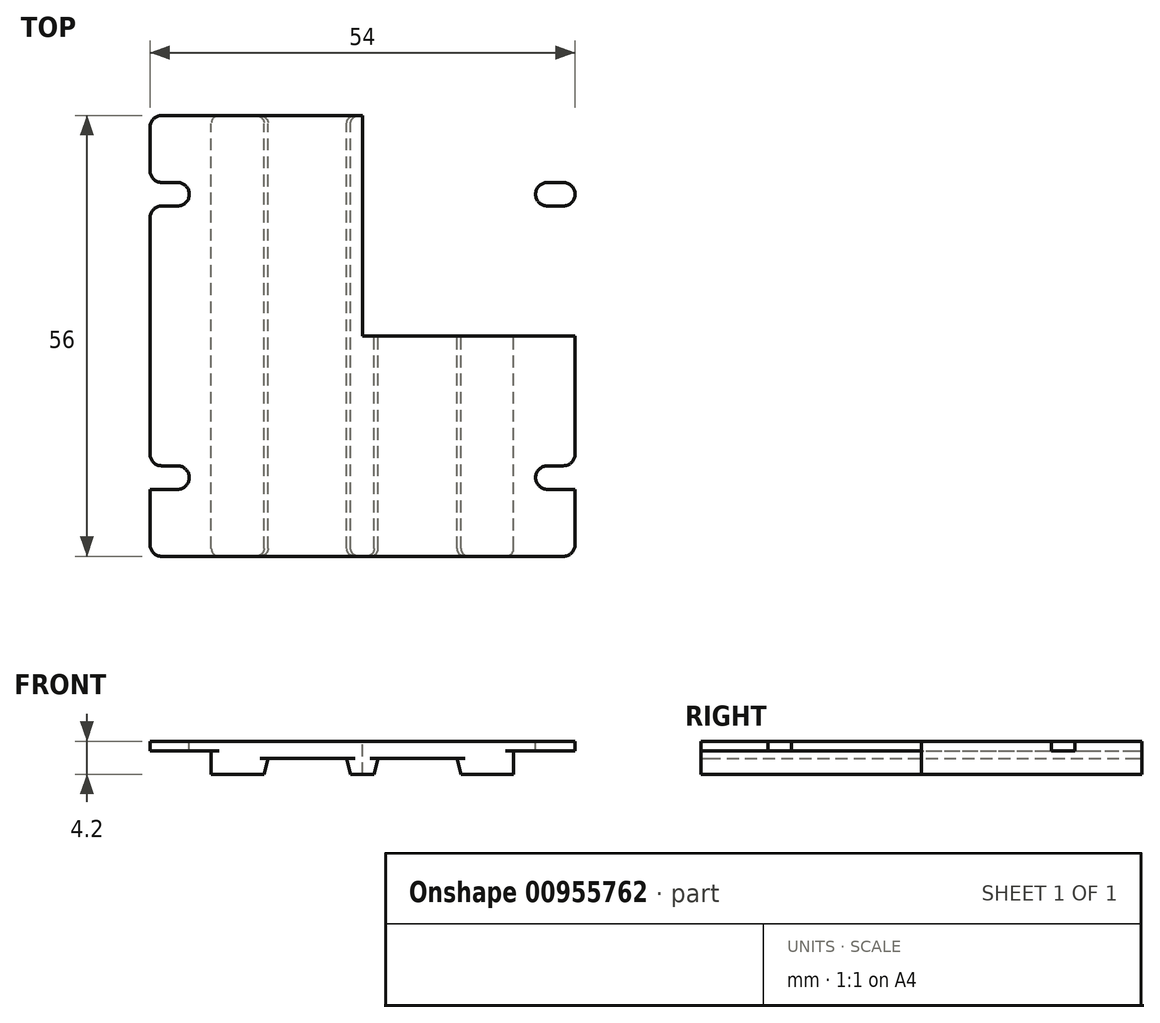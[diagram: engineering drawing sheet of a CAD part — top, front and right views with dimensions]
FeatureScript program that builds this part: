
annotation { "Feature Type Name" : "Feature", "Feature Type Description" : "" }
export const myFeature = defineFeature(function(context is Context, id is Id, definition is map)
    precondition{}
    {
        {
            var Q0;
            Q0=qCreatedBy(makeId("Front.planeOp"),FACE);
            var sketch = newSketch(context, id + "F0", { "sketchPlane" : qUnion([Q0])});
            skLineSegment(sketch, "E0", {"start": v(0, 0) * mm, "end": v(1.5, 0) * mm});
            skLineSegment(sketch, "E1", {"start": v(1.5, 0) * mm, "end": v(2, 2) * mm});
            skLineSegment(sketch, "E2", {"start": v(2, 2) * mm, "end": v(12, 2) * mm});
            skLineSegment(sketch, "E3", {"start": v(12, 2) * mm, "end": v(12.5, 0) * mm});
            skLineSegment(sketch, "E4", {"start": v(12.5, 0) * mm, "end": v(19.2, 0) * mm});
            skLineSegment(sketch, "E5", {"start": v(19.2, 0) * mm, "end": v(19.2, 3) * mm});
            skLineSegment(sketch, "E6", {"start": v(19.2, 3) * mm, "end": v(27, 3) * mm});
            skLineSegment(sketch, "E7", {"start": v(27, 3) * mm, "end": v(27, 4.2) * mm});
            skLineSegment(sketch, "E8", {"start": v(27, 4.2) * mm, "end": v(0, 4.2) * mm});
            skLineSegment(sketch, "E9", {"start": v(0, 4.2) * mm, "end": v(0, 0) * mm});
            skLineSegment(sketch, "E10.MirrorCS", {"start": v(-27, 4.2) * mm, "end": v(0, 4.2) * mm});
            skLineSegment(sketch, "E11.MirrorCS", {"start": v(-27, 3) * mm, "end": v(-27, 4.2) * mm});
            skLineSegment(sketch, "E12.MirrorCS", {"start": v(-19.2, 3) * mm, "end": v(-27, 3) * mm});
            skLineSegment(sketch, "E13.MirrorCS", {"start": v(-19.2, 0) * mm, "end": v(-19.2, 3) * mm});
            skLineSegment(sketch, "E14.MirrorCS", {"start": v(-12.5, 0) * mm, "end": v(-19.2, 0) * mm});
            skLineSegment(sketch, "E15.MirrorCS", {"start": v(-12, 2) * mm, "end": v(-12.5, 0) * mm});
            skLineSegment(sketch, "E16.MirrorCS", {"start": v(-2, 2) * mm, "end": v(-12, 2) * mm});
            skLineSegment(sketch, "E17.MirrorCS", {"start": v(-1.5, 0) * mm, "end": v(-2, 2) * mm});
            skLineSegment(sketch, "E18.MirrorCS", {"start": v(0, 0) * mm, "end": v(-1.5, 0) * mm});
            skSolve(sketch);
        }
        {
            var Q0;
            Q0=makeQuery(id+"F0.imprint","IMPRINT",FACE,{"disambiguationData":[TD([[makeQuery(id+"F0.imprint","IMPRINT",EDGE,{"derivedFrom":sQuery(id+"F0.wireOp",EDGE,"E9")}),-1.0]])]});
            var Q1;
            Q1=makeQuery(id+"F0.imprint","IMPRINT",FACE,{"disambiguationData":[TD([[makeQuery(id+"F0.imprint","IMPRINT",EDGE,{"derivedFrom":sQuery(id+"F0.wireOp",EDGE,"E0")}),1.0]])]});
            extrude(context, id + "F1", {"entities" : qUnion([Q0, Q1]), "depth" : 56 * mm, "offsetDistance" : 25 * mm});
        }
        {
            var Q0;
            Q0=makeQuery(id+"F1.opExtrude","SWEPT_FACE",FACE,{"disambiguationData":[OSD([sQuery(id+"F0.wireOp",EDGE,"E8"),sQuery(id+"F0.wireOp",EDGE,"E10.MirrorCS")])]});
            var sketch = newSketch(context, id + "F2", { "sketchPlane" : qUnion([Q0])});
            skPoint(sketch, "E19", {"position": v(-22, -10) * mm});
            skPoint(sketch, "E20", {"position": v(-24, -46) * mm});
            skPoint(sketch, "E21.MirrorP", {"position": v(22, -10) * mm});
            skPoint(sketch, "E22.MirrorP", {"position": v(24, -46) * mm});
            skLineSegment(sketch, "E23", {"start": v(-22, -10) * mm, "end": v(-22, -10) * mm});
            skLineSegment(sketch, "E24", {"start": v(-23.5, -8.5) * mm, "end": v(-27, -8.5) * mm});
            skLineSegment(sketch, "E25", {"start": v(-23.5, -11.5) * mm, "end": v(-27, -11.5) * mm});
            skPoint(sketch, "E26.visualSharp", {"position": v(-22, -11.5) * mm});
            skArc(sketch, "E26.filletArc", {"start": v(-23.5, -11.5) * mm, "mid": v(-22.44, -11.06) * mm, "end": v(-22, -10) * mm});
            skPoint(sketch, "E27.visualSharp", {"position": v(-22, -8.5) * mm});
            skArc(sketch, "E27.filletArc", {"start": v(-22, -10) * mm, "mid": v(-22.44, -8.94) * mm, "end": v(-23.5, -8.5) * mm});
            skLineSegment(sketch, "E28", {"start": v(-27, -28) * mm, "end": v(27, -28) * mm});
            skLineSegment(sketch, "E29.MirrorCS", {"start": v(-23.5, -44.5) * mm, "end": v(-27, -44.5) * mm});
            skArc(sketch, "E30.MirrorCS", {"start": v(-23.5, -44.5) * mm, "mid": v(-22.44, -44.94) * mm, "end": v(-22, -46) * mm});
            skArc(sketch, "E31.MirrorCS", {"start": v(-22, -46) * mm, "mid": v(-22.44, -47.06) * mm, "end": v(-23.5, -47.5) * mm});
            skLineSegment(sketch, "E32.MirrorCS", {"start": v(-23.5, -47.5) * mm, "end": v(-27, -47.5) * mm});
            skLineSegment(sketch, "E33", {"start": v(0, -56) * mm, "end": v(0, 0) * mm});
            skLineSegment(sketch, "E34.MirrorCS", {"start": v(23.5, -47.5) * mm, "end": v(27, -47.5) * mm});
            skArc(sketch, "E35.MirrorCS", {"start": v(22, -46) * mm, "mid": v(22.44, -47.06) * mm, "end": v(23.5, -47.5) * mm});
            skArc(sketch, "E36.MirrorCS", {"start": v(23.5, -44.5) * mm, "mid": v(22.44, -44.94) * mm, "end": v(22, -46) * mm});
            skLineSegment(sketch, "E37.MirrorCS", {"start": v(23.5, -44.5) * mm, "end": v(27, -44.5) * mm});
            skArc(sketch, "E38.MirrorCS", {"start": v(23.5, -11.5) * mm, "mid": v(22.44, -11.06) * mm, "end": v(22, -10) * mm});
            skLineSegment(sketch, "E39.MirrorCS", {"start": v(23.5, -11.5) * mm, "end": v(27, -11.5) * mm});
            skLineSegment(sketch, "E40.MirrorCS", {"start": v(23.5, -8.5) * mm, "end": v(27, -8.5) * mm});
            skArc(sketch, "E41.MirrorCS", {"start": v(22, -10) * mm, "mid": v(22.44, -8.94) * mm, "end": v(23.5, -8.5) * mm});
            skSolve(sketch);
        }
        {
            var Q0;
            {var subQ1=sQuery(id+"F2.wireOp",EDGE,"E34.MirrorCS");Q0=makeQuery(id+"F2.imprint","IMPRINT",FACE,{"disambiguationData":[TD([[makeQuery(id+"F2.imprint","IMPRINT",EDGE,{"derivedFrom":subQ1}),1.0]])]});}
            var Q1;
            Q1=makeQuery(id+"F2.imprint","IMPRINT",FACE,{"disambiguationData":[TD([[makeQuery(id+"F2.imprint","IMPRINT",EDGE,{"derivedFrom":sQuery(id+"F2.wireOp",EDGE,"E38.MirrorCS")}),-1.0]])]});
            var Q2;
            {var subQ1=sQuery(id+"F2.wireOp",EDGE,"E24");Q2=makeQuery(id+"F2.imprint","IMPRINT",FACE,{"disambiguationData":[TD([[makeQuery(id+"F2.imprint","IMPRINT",EDGE,{"derivedFrom":subQ1}),1.0]])]});}
            var Q3;
            {var subQ1=sQuery(id+"F2.wireOp",EDGE,"E29.MirrorCS");Q3=makeQuery(id+"F2.imprint","IMPRINT",FACE,{"disambiguationData":[TD([[makeQuery(id+"F2.imprint","IMPRINT",EDGE,{"derivedFrom":subQ1}),1.0]])]});}
            extrude(context, id + "F3", {"entities" : qUnion([Q0, Q1, Q2, Q3]), "operationType" : NewBodyOperationType.REMOVE, "oppositeDirection" : true, "depth" : 25 * mm, "offsetDistance" : 25 * mm});
        }
        {
            var Q0;
            Q0=makeQuery(id+"F3.boolean.opBoolean","COPY",EDGE,{"derivedFrom":makeQuery(id+"F3.opExtrude","SWEPT_EDGE",EDGE,{"disambiguationData":[OSD([sQuery(id+"F0.wireOp",EDGE,"E10.MirrorCS"),sQuery(id+"F0.wireOp",EDGE,"E11.MirrorCS"),sQuery(id+"F2.wireOp",EDGE,"E32.MirrorCS")])]})});
            var Q1;
            Q1=makeQuery(id+"F3.boolean.opBoolean","COPY",EDGE,{"derivedFrom":makeQuery(id+"F3.opExtrude","SWEPT_EDGE",EDGE,{"disambiguationData":[OSD([sQuery(id+"F0.wireOp",EDGE,"E10.MirrorCS"),sQuery(id+"F0.wireOp",EDGE,"E11.MirrorCS"),sQuery(id+"F2.wireOp",EDGE,"E29.MirrorCS")])]})});
            var Q2;
            Q2=makeQuery(id+"F3.boolean.opBoolean","COPY",EDGE,{"derivedFrom":makeQuery(id+"F3.opExtrude","SWEPT_EDGE",EDGE,{"disambiguationData":[OSD([sQuery(id+"F0.wireOp",EDGE,"E7"),sQuery(id+"F0.wireOp",EDGE,"E8"),sQuery(id+"F2.wireOp",EDGE,"E34.MirrorCS")])]})});
            var Q3;
            Q3=makeQuery(id+"F3.boolean.opBoolean","COPY",EDGE,{"derivedFrom":makeQuery(id+"F3.opExtrude","SWEPT_EDGE",EDGE,{"disambiguationData":[OSD([sQuery(id+"F0.wireOp",EDGE,"E7"),sQuery(id+"F0.wireOp",EDGE,"E8"),sQuery(id+"F2.wireOp",EDGE,"E37.MirrorCS")])]})});
            var Q4;
            Q4=makeQuery(id+"F3.boolean.opBoolean","COPY",EDGE,{"derivedFrom":makeQuery(id+"F3.opExtrude","SWEPT_EDGE",EDGE,{"disambiguationData":[OSD([sQuery(id+"F0.wireOp",EDGE,"E7"),sQuery(id+"F0.wireOp",EDGE,"E8"),sQuery(id+"F2.wireOp",EDGE,"E39.MirrorCS")])]})});
            var Q5;
            Q5=makeQuery(id+"F3.boolean.opBoolean","COPY",EDGE,{"derivedFrom":makeQuery(id+"F3.opExtrude","SWEPT_EDGE",EDGE,{"disambiguationData":[OSD([sQuery(id+"F0.wireOp",EDGE,"E7"),sQuery(id+"F0.wireOp",EDGE,"E8"),sQuery(id+"F2.wireOp",EDGE,"E40.MirrorCS")])]})});
            var Q6;
            Q6=makeQuery(id+"F3.boolean.opBoolean","COPY",EDGE,{"derivedFrom":makeQuery(id+"F3.opExtrude","SWEPT_EDGE",EDGE,{"disambiguationData":[OSD([sQuery(id+"F0.wireOp",EDGE,"E10.MirrorCS"),sQuery(id+"F0.wireOp",EDGE,"E11.MirrorCS"),sQuery(id+"F2.wireOp",EDGE,"E25")])]})});
            var Q7;
            Q7=makeQuery(id+"F3.boolean.opBoolean","COPY",EDGE,{"derivedFrom":makeQuery(id+"F3.opExtrude","SWEPT_EDGE",EDGE,{"disambiguationData":[OSD([sQuery(id+"F0.wireOp",EDGE,"E10.MirrorCS"),sQuery(id+"F0.wireOp",EDGE,"E11.MirrorCS"),sQuery(id+"F2.wireOp",EDGE,"E24")])]})});
            var Q8;
            Q8=makeQuery(id+"F1.opExtrude","CAP_EDGE",EDGE,{"disambiguationData":[OSD([sQuery(id+"F0.wireOp",EDGE,"E7")])],"isStart":false});
            var Q9;
            Q9=makeQuery(id+"F1.opExtrude","CAP_EDGE",EDGE,{"disambiguationData":[OSD([sQuery(id+"F0.wireOp",EDGE,"E11.MirrorCS")])],"isStart":false});
            var Q10;
            Q10=makeQuery(id+"F1.opExtrude","CAP_EDGE",EDGE,{"disambiguationData":[OSD([sQuery(id+"F0.wireOp",EDGE,"E11.MirrorCS")])],"isStart":true});
            var Q11;
            Q11=makeQuery(id+"F1.opExtrude","CAP_EDGE",EDGE,{"disambiguationData":[OSD([sQuery(id+"F0.wireOp",EDGE,"E7")])],"isStart":true});
            fillet(context, id + "F4", {"entities" : qUnion([Q0, Q1, Q2, Q3, Q4, Q5, Q6, Q7, Q8, Q9, Q10, Q11]), "radius" : 1.5 * mm, "tangentPropagation" : true, "allowEdgeOverflow" : false});
        }
        {
            var Q0;
            Q0=makeQuery(id+"F1.opExtrude","CAP_EDGE",EDGE,{"disambiguationData":[OSD([sQuery(id+"F0.wireOp",EDGE,"E3")])],"isStart":true});
            var Q1;
            Q1=makeQuery(id+"F1.opExtrude","CAP_EDGE",EDGE,{"disambiguationData":[OSD([sQuery(id+"F0.wireOp",EDGE,"E5")])],"isStart":true});
            var Q2;
            Q2=makeQuery(id+"F1.opExtrude","CAP_EDGE",EDGE,{"disambiguationData":[OSD([sQuery(id+"F0.wireOp",EDGE,"E1")])],"isStart":true});
            var Q3;
            Q3=makeQuery(id+"F1.opExtrude","CAP_EDGE",EDGE,{"disambiguationData":[OSD([sQuery(id+"F0.wireOp",EDGE,"E17.MirrorCS")])],"isStart":true});
            var Q4;
            Q4=makeQuery(id+"F1.opExtrude","CAP_EDGE",EDGE,{"disambiguationData":[OSD([sQuery(id+"F0.wireOp",EDGE,"E15.MirrorCS")])],"isStart":true});
            var Q5;
            Q5=makeQuery(id+"F1.opExtrude","CAP_EDGE",EDGE,{"disambiguationData":[OSD([sQuery(id+"F0.wireOp",EDGE,"E13.MirrorCS")])],"isStart":true});
            var Q6;
            Q6=makeQuery(id+"F1.opExtrude","CAP_EDGE",EDGE,{"disambiguationData":[OSD([sQuery(id+"F0.wireOp",EDGE,"E13.MirrorCS")])],"isStart":false});
            var Q7;
            Q7=makeQuery(id+"F1.opExtrude","CAP_EDGE",EDGE,{"disambiguationData":[OSD([sQuery(id+"F0.wireOp",EDGE,"E15.MirrorCS")])],"isStart":false});
            var Q8;
            Q8=makeQuery(id+"F1.opExtrude","CAP_EDGE",EDGE,{"disambiguationData":[OSD([sQuery(id+"F0.wireOp",EDGE,"E17.MirrorCS")])],"isStart":false});
            var Q9;
            Q9=makeQuery(id+"F1.opExtrude","CAP_EDGE",EDGE,{"disambiguationData":[OSD([sQuery(id+"F0.wireOp",EDGE,"E1")])],"isStart":false});
            var Q10;
            Q10=makeQuery(id+"F1.opExtrude","CAP_EDGE",EDGE,{"disambiguationData":[OSD([sQuery(id+"F0.wireOp",EDGE,"E3")])],"isStart":false});
            var Q11;
            Q11=makeQuery(id+"F1.opExtrude","CAP_EDGE",EDGE,{"disambiguationData":[OSD([sQuery(id+"F0.wireOp",EDGE,"E5")])],"isStart":false});
            fillet(context, id + "F5", {"entities" : qUnion([Q0, Q1, Q2, Q3, Q4, Q5, Q6, Q7, Q8, Q9, Q10, Q11]), "radius" : 1 * mm, "tangentPropagation" : true, "allowEdgeOverflow" : false});
        }
    });
